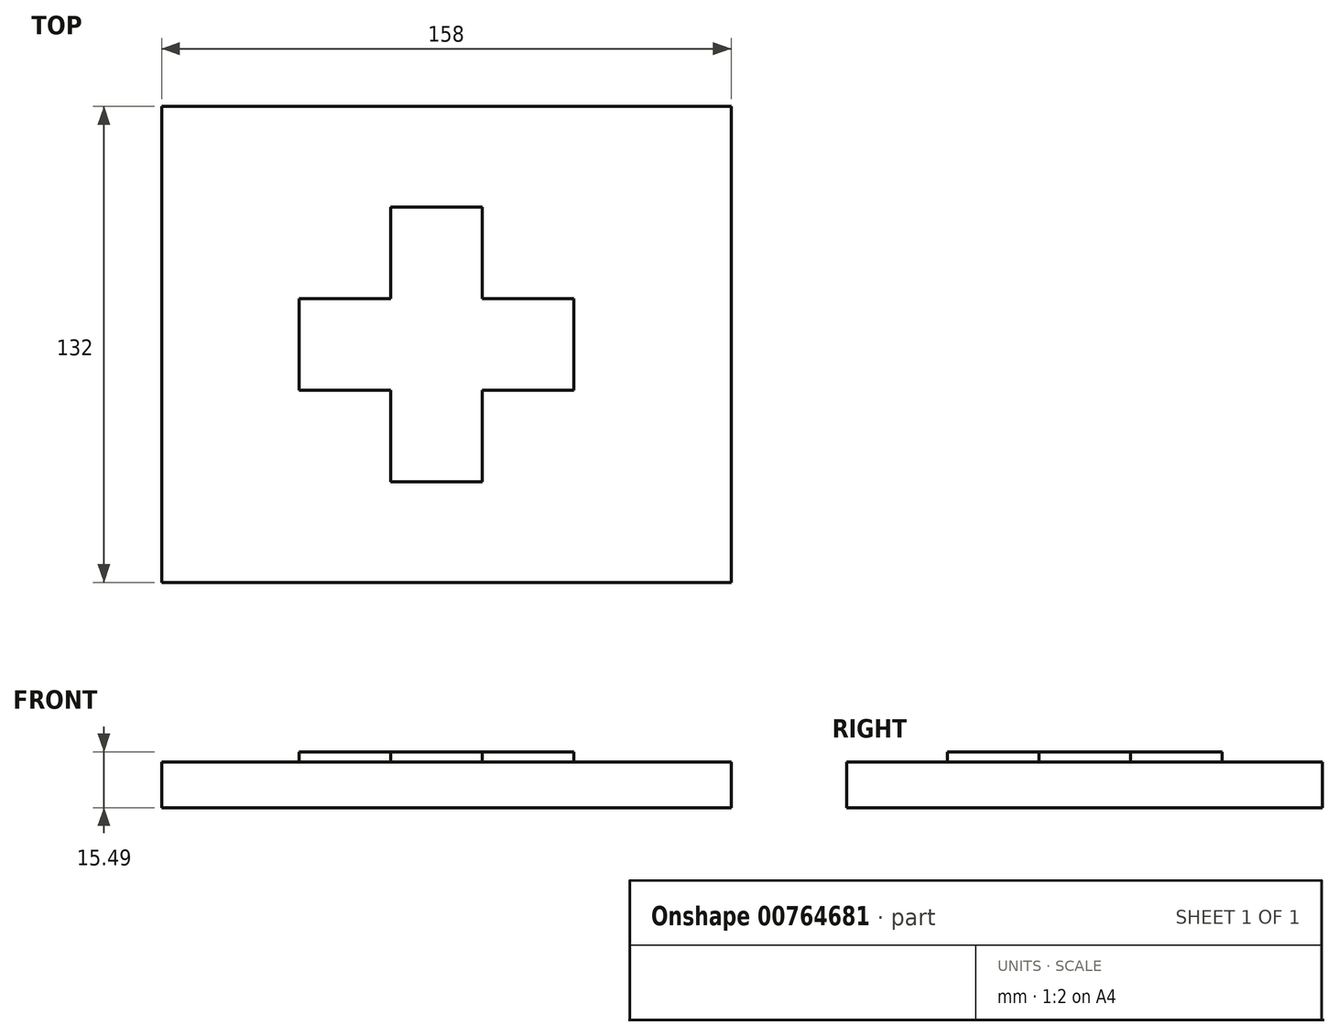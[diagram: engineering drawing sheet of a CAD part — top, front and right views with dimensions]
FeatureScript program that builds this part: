
annotation { "Feature Type Name" : "Feature", "Feature Type Description" : "" }
export const myFeature = defineFeature(function(context is Context, id is Id, definition is map)
    precondition{}
    {
        {
            var Q0;
            Q0=qCreatedBy(makeId("Top.planeOp"),FACE);
            var sketch = newSketch(context, id + "F0", { "sketchPlane" : qUnion([Q0])});
            skLineSegment(sketch, "E0.bottom", {"start": v(-158, 0) * mm, "end": v(0, 0) * mm});
            skLineSegment(sketch, "E0.top", {"start": v(-158, -132) * mm, "end": v(0, -132) * mm});
            skLineSegment(sketch, "E0.left", {"start": v(-158, 0) * mm, "end": v(-158, -132) * mm});
            skLineSegment(sketch, "E0.right", {"start": v(0, 0) * mm, "end": v(0, -132) * mm});
            skSolve(sketch);
        }
        {
            var Q0;
            Q0=makeQuery(id+"F0.imprint","IMPRINT",FACE,{"disambiguationData":[TD([[makeQuery(id+"F0.imprint","IMPRINT",EDGE,{"derivedFrom":sQuery(id+"F0.wireOp",EDGE,"E0.bottom")}),-1.0]])]});
            extrude(context, id + "F1", {"entities" : qUnion([Q0]), "depth" : 12.7 * mm, "offsetDistance" : 25.4 * mm});
        }
        {
            var Q0;
            Q0=makeQuery(id+"F1.opExtrude","CAP_FACE",FACE,{"disambiguationData":[OSD([sQuery(id+"F0.wireOp",EDGE,"E0.bottom"),sQuery(id+"F0.wireOp",EDGE,"E0.top"),sQuery(id+"F0.wireOp",EDGE,"E0.left"),sQuery(id+"F0.wireOp",EDGE,"E0.right")])],"isStart":false});
            var sketch = newSketch(context, id + "F2", { "sketchPlane" : qUnion([Q0])});
            skLineSegment(sketch, "E1", {"start": v(-119.9, -78.66) * mm, "end": v(-94.5, -78.66) * mm});
            skLineSegment(sketch, "E2", {"start": v(-94.5, -78.66) * mm, "end": v(-94.5, -104.06) * mm});
            skLineSegment(sketch, "E3", {"start": v(-94.5, -104.06) * mm, "end": v(-69.1, -104.06) * mm});
            skLineSegment(sketch, "E4", {"start": v(-69.1, -104.06) * mm, "end": v(-69.1, -78.66) * mm});
            skLineSegment(sketch, "E5", {"start": v(-69.1, -78.66) * mm, "end": v(-43.7, -78.66) * mm});
            skLineSegment(sketch, "E6", {"start": v(-43.7, -78.66) * mm, "end": v(-43.7, -53.26) * mm});
            skLineSegment(sketch, "E7", {"start": v(-43.7, -53.26) * mm, "end": v(-69.1, -53.26) * mm});
            skLineSegment(sketch, "E8", {"start": v(-69.1, -53.26) * mm, "end": v(-69.1, -27.86) * mm});
            skLineSegment(sketch, "E9", {"start": v(-69.1, -27.86) * mm, "end": v(-94.5, -27.86) * mm});
            skLineSegment(sketch, "E10", {"start": v(-94.5, -27.86) * mm, "end": v(-94.5, -53.26) * mm});
            skLineSegment(sketch, "E11", {"start": v(-94.5, -53.26) * mm, "end": v(-119.9, -53.26) * mm});
            skLineSegment(sketch, "E12", {"start": v(-119.9, -53.26) * mm, "end": v(-119.9, -78.66) * mm});
            skPoint(sketch, "E13.endSnap0", {"position": v(0, -66) * mm});
            skSolve(sketch);
        }
        {
            var Q0;
            Q0 = qSketchRegion(id + "F2", true);
            extrude(context, id + "F3", {"entities" : qUnion([Q0]), "operationType" : NewBodyOperationType.ADD, "depth" : 2.8 * mm, "offsetDistance" : 25.4 * mm});
        }
    });
